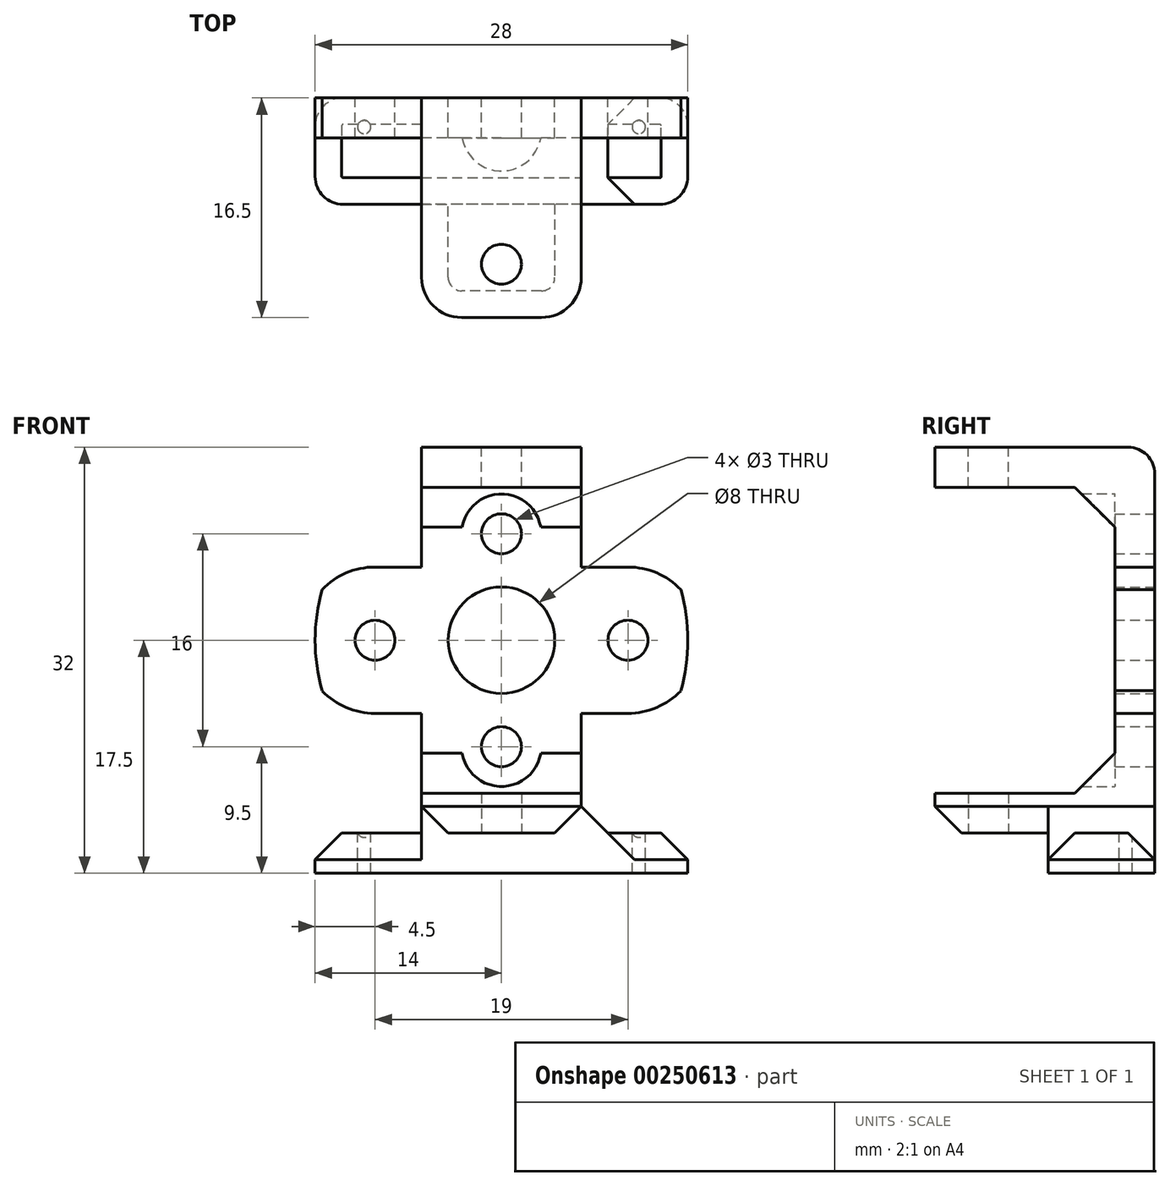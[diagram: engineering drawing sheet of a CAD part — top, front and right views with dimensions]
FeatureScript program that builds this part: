
annotation { "Feature Type Name" : "Feature", "Feature Type Description" : "" }
export const myFeature = defineFeature(function(context is Context, id is Id, definition is map)
    precondition{}
    {
        {
            var Q0;
            Q0=qCreatedBy(makeId("Front.planeOp"),FACE);
            var sketch = newSketch(context, id + "F0", { "sketchPlane" : qUnion([Q0])});
            skCircle(sketch, "E0", {"center": v(0, 0) * mm, "radius": 4.5 * mm});
            skCircle(sketch, "E1", {"center": v(9.5, 0) * mm, "radius": 1.5 * mm});
            skCircle(sketch, "E2.MirrorC", {"center": v(-9.5, 0) * mm, "radius": 1.5 * mm});
            skArc(sketch, "E3.0", {"start": v(9.5, -5.5) * mm, "mid": v(11.66, -5.06) * mm, "end": v(13.47, -3.8) * mm});
            skLineSegment(sketch, "E4", {"start": v(9.5, 7.45) * mm, "end": v(9.5, -7.59) * mm, "construction": true});
            skLineSegment(sketch, "E5", {"start": v(9.5, -5.5) * mm, "end": v(0, -5.5) * mm});
            skLineSegment(sketch, "E6.MirrorCS", {"start": v(9.5, 5.5) * mm, "end": v(0, 5.5) * mm});
            skArc(sketch, "E7.MirrorCS", {"start": v(-9.5, -5.5) * mm, "mid": v(-11.66, -5.06) * mm, "end": v(-13.47, -3.8) * mm});
            skLineSegment(sketch, "E8.MirrorCS", {"start": v(-9.5, 5.5) * mm, "end": v(0, 5.5) * mm});
            skLineSegment(sketch, "E9.MirrorCS", {"start": v(-9.5, -5.5) * mm, "end": v(0, -5.5) * mm});
            skArc(sketch, "E10", {"start": v(-13.47, 3.8) * mm, "mid": v(-14, 0) * mm, "end": v(-13.47, -3.8) * mm});
            skArc(sketch, "E11.trimOffspring", {"start": v(13.47, -3.8) * mm, "mid": v(14, 0) * mm, "end": v(13.47, 3.8) * mm});
            skArc(sketch, "E12.trimOffspring", {"start": v(-13.47, 3.8) * mm, "mid": v(-11.66, 5.06) * mm, "end": v(-9.5, 5.5) * mm});
            skArc(sketch, "E13.trimOffspring", {"start": v(13.47, 3.8) * mm, "mid": v(11.66, 5.06) * mm, "end": v(9.5, 5.5) * mm});
            skSolve(sketch);
        }
        {
            var Q0;
            Q0=qSketchRegion(id+"F0",true);
            extrude(context, id + "F1", {"entities" : qUnion([Q0]), "depth" : 3 * mm});
        }
        {
            var Q0;
            Q0=makeQuery(id+"F1.opExtrude","CAP_FACE",FACE,{"disambiguationData":[OSD([sQuery(id+"F0.wireOp",EDGE,"E0"),sQuery(id+"F0.wireOp",EDGE,"E1"),sQuery(id+"F0.wireOp",EDGE,"E2.MirrorC"),sQuery(id+"F0.wireOp",EDGE,"E3.0"),sQuery(id+"F0.wireOp",EDGE,"E5"),sQuery(id+"F0.wireOp",EDGE,"E6.MirrorCS"),sQuery(id+"F0.wireOp",EDGE,"E7.MirrorCS"),sQuery(id+"F0.wireOp",EDGE,"E8.MirrorCS"),sQuery(id+"F0.wireOp",EDGE,"E9.MirrorCS")])],"isStart":false});
            var sketch = newSketch(context, id + "F2", { "sketchPlane" : qUnion([Q0])});
            skLineSegment(sketch, "E14.rect.bottom", {"start": v(6, -14.5) * mm, "end": v(-6, -14.5) * mm});
            skLineSegment(sketch, "E14.rect.top", {"start": v(6, 14.5) * mm, "end": v(-6, 14.5) * mm});
            skLineSegment(sketch, "E14.rect.left", {"start": v(6, -14.5) * mm, "end": v(6, 14.5) * mm});
            skLineSegment(sketch, "E14.rect.right", {"start": v(-6, -14.5) * mm, "end": v(-6, 14.5) * mm});
            skPoint(sketch, "E14.rect.middle", {"position": v(0, 0) * mm});
            skSolve(sketch);
        }
        {
            var Q0;
            Q0=qSketchRegion(id+"F2",true);
            extrude(context, id + "F3", {"entities" : qUnion([Q0]), "operationType" : NewBodyOperationType.ADD, "oppositeDirection" : true, "depth" : 3 * mm});
        }
        {
            var Q0;
            Q0=makeQuery(id+"F3.opExtrude","SWEPT_FACE",FACE,{"disambiguationData":[OSD([sQuery(id+"F2.wireOp",EDGE,"E14.rect.bottom")])]});
            var sketch = newSketch(context, id + "F4", { "sketchPlane" : qUnion([Q0])});
            skLineSegment(sketch, "E15.bottom", {"start": v(-6, 0) * mm, "end": v(6, 0) * mm, "construction": true});
            skCircle(sketch, "E16", {"center": v(0, 12.5) * mm, "radius": 1.5 * mm});
            skLineSegment(sketch, "E17.bottom", {"start": v(-6, 0) * mm, "end": v(6, 0) * mm});
            skLineSegment(sketch, "E17.top", {"start": v(-3, 16.5) * mm, "end": v(3, 16.5) * mm});
            skLineSegment(sketch, "E17.left", {"start": v(-6, 0) * mm, "end": v(-6, 13.5) * mm});
            skLineSegment(sketch, "E17.right", {"start": v(6, 0) * mm, "end": v(6, 13.5) * mm});
            skPoint(sketch, "E18.visualSharp", {"position": v(-6, 16.5) * mm});
            skArc(sketch, "E18.filletArc", {"start": v(-3, 16.5) * mm, "mid": v(-5.12, 15.62) * mm, "end": v(-6, 13.5) * mm});
            skPoint(sketch, "E19.visualSharp", {"position": v(6, 16.5) * mm});
            skArc(sketch, "E19.filletArc", {"start": v(6, 13.5) * mm, "mid": v(5.12, 15.62) * mm, "end": v(3, 16.5) * mm});
            skSolve(sketch);
        }
        {
            var Q0;
            Q0=qSketchRegion(id+"F4",true);
            extrude(context, id + "F5", {"entities" : qUnion([Q0]), "oppositeDirection" : true, "depth" : 3 * mm});
        }
        {
            var Q0;
            Q0=makeQuery(id+"F3.boolean.opBoolean","MERGE",FACE,{"derivedFrom":[makeQuery(id+"F1.opExtrude","CAP_FACE",FACE,{"disambiguationData":[OSD([sQuery(id+"F0.wireOp",EDGE,"E0"),sQuery(id+"F0.wireOp",EDGE,"E1"),sQuery(id+"F0.wireOp",EDGE,"E2.MirrorC"),sQuery(id+"F0.wireOp",EDGE,"E3.0"),sQuery(id+"F0.wireOp",EDGE,"E5"),sQuery(id+"F0.wireOp",EDGE,"E6.MirrorCS"),sQuery(id+"F0.wireOp",EDGE,"E7.MirrorCS"),sQuery(id+"F0.wireOp",EDGE,"E8.MirrorCS"),sQuery(id+"F0.wireOp",EDGE,"E9.MirrorCS")])],"isStart":true}),makeQuery(id+"F3.opExtrude","CAP_FACE",FACE,{"disambiguationData":[OSD([sQuery(id+"F2.wireOp",EDGE,"E14.rect.bottom"),sQuery(id+"F2.wireOp",EDGE,"E14.rect.top"),sQuery(id+"F2.wireOp",EDGE,"E14.rect.left"),sQuery(id+"F2.wireOp",EDGE,"E14.rect.right")])],"isStart":false})]});
            var sketch = newSketch(context, id + "F6", { "sketchPlane" : qUnion([Q0])});
            skCircle(sketch, "E20", {"center": v(0, 0) * mm, "radius": 4 * mm});
            skCircle(sketch, "E21", {"center": v(0, 8) * mm, "radius": 1.5 * mm});
            skCircle(sketch, "E22.MirrorC", {"center": v(0, -8) * mm, "radius": 1.5 * mm});
            skSolve(sketch);
        }
        {
            var Q0;
            Q0=qSketchRegion(id+"F6",true);
            extrude(context, id + "F7", {"entities" : qUnion([Q0]), "operationType" : NewBodyOperationType.REMOVE, "endBound" : BoundingType.UP_TO_NEXT, "oppositeDirection" : true, "depth" : 25 * mm});
        }
        {
            var Q0;
            Q0=makeQuery(id+"F5.opExtrude","SWEPT_BODY",BODY,{"disambiguationData":[OSD([sQuery(id+"F4.wireOp",EDGE,"E16"),sQuery(id+"F4.wireOp",EDGE,"E17.bottom"),sQuery(id+"F4.wireOp",EDGE,"E17.top"),sQuery(id+"F4.wireOp",EDGE,"E17.left"),sQuery(id+"F4.wireOp",EDGE,"E17.right"),sQuery(id+"F4.wireOp",EDGE,"E18.filletArc"),sQuery(id+"F4.wireOp",EDGE,"E19.filletArc")])]});
            var Q1;
            Q1=qCreatedBy(makeId("Top.planeOp"),FACE);
            mirror(context, id + "F8", {"operationType" : NewBodyOperationType.ADD, "entities" : qUnion([Q0]), "mirrorPlane" : qUnion([Q1])});
        }
        {
            var Q0;
            Q0=makeQuery(id+"F3.opExtrude","CAP_EDGE",EDGE,{"disambiguationData":[OSD([sQuery(id+"F2.wireOp",EDGE,"E14.rect.top")])],"isStart":false});
            fillet(context, id + "F9", {"entities" : qUnion([Q0]), "radius" : 2 * mm, "tangentPropagation" : true, "allowEdgeOverflow" : false});
        }
        {
            var Q0;
            Q0=makeQuery(id+"F8.boolean.opBoolean","INTERSECT",EDGE,{"derivedFrom":[makeQuery(id+"F3.boolean.opBoolean","MERGE",FACE,{"derivedFrom":[makeQuery(id+"F1.opExtrude","CAP_FACE",FACE,{"disambiguationData":[OSD([sQuery(id+"F0.wireOp",EDGE,"E0"),sQuery(id+"F0.wireOp",EDGE,"E1"),sQuery(id+"F0.wireOp",EDGE,"E2.MirrorC"),sQuery(id+"F0.wireOp",EDGE,"E3.0"),sQuery(id+"F0.wireOp",EDGE,"E5"),sQuery(id+"F0.wireOp",EDGE,"E6.MirrorCS"),sQuery(id+"F0.wireOp",EDGE,"E7.MirrorCS"),sQuery(id+"F0.wireOp",EDGE,"E8.MirrorCS"),sQuery(id+"F0.wireOp",EDGE,"E9.MirrorCS"),sQuery(id+"F0.wireOp",EDGE,"E10"),sQuery(id+"F0.wireOp",EDGE,"E11.trimOffspring"),sQuery(id+"F0.wireOp",EDGE,"E12.trimOffspring"),sQuery(id+"F0.wireOp",EDGE,"E13.trimOffspring")])],"isStart":false}),makeQuery(id+"F3.opExtrude","CAP_FACE",FACE,{"disambiguationData":[OSD([sQuery(id+"F2.wireOp",EDGE,"E14.rect.bottom"),sQuery(id+"F2.wireOp",EDGE,"E14.rect.top"),sQuery(id+"F2.wireOp",EDGE,"E14.rect.left"),sQuery(id+"F2.wireOp",EDGE,"E14.rect.right")])],"isStart":true})]}),makeQuery(id+"F8.opPattern","COPY",FACE,{"derivedFrom":makeQuery(id+"F5.opExtrude","CAP_FACE",FACE,{"disambiguationData":[OSD([sQuery(id+"F4.wireOp",EDGE,"E16"),sQuery(id+"F4.wireOp",EDGE,"E17.bottom"),sQuery(id+"F4.wireOp",EDGE,"E17.top"),sQuery(id+"F4.wireOp",EDGE,"E17.left"),sQuery(id+"F4.wireOp",EDGE,"E17.right"),sQuery(id+"F4.wireOp",EDGE,"E18.filletArc"),sQuery(id+"F4.wireOp",EDGE,"E19.filletArc")])],"isStart":false}),"instanceName":"1"})]});
            var Q1;
            Q1=makeQuery(id+"F8.boolean.opBoolean","INTERSECT",EDGE,{"derivedFrom":[makeQuery(id+"F5.opExtrude","CAP_FACE",FACE,{"disambiguationData":[OSD([sQuery(id+"F4.wireOp",EDGE,"E16"),sQuery(id+"F4.wireOp",EDGE,"E17.bottom"),sQuery(id+"F4.wireOp",EDGE,"E17.top"),sQuery(id+"F4.wireOp",EDGE,"E17.left"),sQuery(id+"F4.wireOp",EDGE,"E17.right"),sQuery(id+"F4.wireOp",EDGE,"E18.filletArc"),sQuery(id+"F4.wireOp",EDGE,"E19.filletArc")])],"isStart":false}),makeQuery(id+"F3.boolean.opBoolean","MERGE",FACE,{"derivedFrom":[makeQuery(id+"F1.opExtrude","CAP_FACE",FACE,{"disambiguationData":[OSD([sQuery(id+"F0.wireOp",EDGE,"E0"),sQuery(id+"F0.wireOp",EDGE,"E1"),sQuery(id+"F0.wireOp",EDGE,"E2.MirrorC"),sQuery(id+"F0.wireOp",EDGE,"E3.0"),sQuery(id+"F0.wireOp",EDGE,"E5"),sQuery(id+"F0.wireOp",EDGE,"E6.MirrorCS"),sQuery(id+"F0.wireOp",EDGE,"E7.MirrorCS"),sQuery(id+"F0.wireOp",EDGE,"E8.MirrorCS"),sQuery(id+"F0.wireOp",EDGE,"E9.MirrorCS"),sQuery(id+"F0.wireOp",EDGE,"E10"),sQuery(id+"F0.wireOp",EDGE,"E11.trimOffspring"),sQuery(id+"F0.wireOp",EDGE,"E12.trimOffspring"),sQuery(id+"F0.wireOp",EDGE,"E13.trimOffspring")])],"isStart":false}),makeQuery(id+"F3.opExtrude","CAP_FACE",FACE,{"disambiguationData":[OSD([sQuery(id+"F2.wireOp",EDGE,"E14.rect.bottom"),sQuery(id+"F2.wireOp",EDGE,"E14.rect.top"),sQuery(id+"F2.wireOp",EDGE,"E14.rect.left"),sQuery(id+"F2.wireOp",EDGE,"E14.rect.right")])],"isStart":true})]})]});
            chamfer(context, id + "F10", {"entities" : qUnion([Q0, Q1]), "width" : 3 * mm, "tangentPropagation" : true});
        }
        {
            var Q0;
            Q0=makeQuery(id+"F3.boolean.opBoolean","MERGE",FACE,{"derivedFrom":[makeQuery(id+"F1.opExtrude","CAP_FACE",FACE,{"disambiguationData":[OSD([sQuery(id+"F0.wireOp",EDGE,"E0"),sQuery(id+"F0.wireOp",EDGE,"E1"),sQuery(id+"F0.wireOp",EDGE,"E2.MirrorC"),sQuery(id+"F0.wireOp",EDGE,"E3.0"),sQuery(id+"F0.wireOp",EDGE,"E5"),sQuery(id+"F0.wireOp",EDGE,"E6.MirrorCS"),sQuery(id+"F0.wireOp",EDGE,"E7.MirrorCS"),sQuery(id+"F0.wireOp",EDGE,"E8.MirrorCS"),sQuery(id+"F0.wireOp",EDGE,"E9.MirrorCS"),sQuery(id+"F0.wireOp",EDGE,"E10"),sQuery(id+"F0.wireOp",EDGE,"E11.trimOffspring"),sQuery(id+"F0.wireOp",EDGE,"E12.trimOffspring"),sQuery(id+"F0.wireOp",EDGE,"E13.trimOffspring")])],"isStart":false}),makeQuery(id+"F3.opExtrude","CAP_FACE",FACE,{"disambiguationData":[OSD([sQuery(id+"F2.wireOp",EDGE,"E14.rect.bottom"),sQuery(id+"F2.wireOp",EDGE,"E14.rect.top"),sQuery(id+"F2.wireOp",EDGE,"E14.rect.left"),sQuery(id+"F2.wireOp",EDGE,"E14.rect.right")])],"isStart":true})]});
            var sketch = newSketch(context, id + "F11", { "sketchPlane" : qUnion([Q0])});
            skCircle(sketch, "E23", {"center": v(0, 8) * mm, "radius": 3 * mm});
            skCircle(sketch, "E24.MirrorC", {"center": v(0, -8) * mm, "radius": 3 * mm});
            skSolve(sketch);
        }
        {
            var Q0;
            Q0=qSketchRegion(id+"F11",true);
            var Q1;
            {var subQ0=sQuery(id+"F2.wireOp",EDGE,"E14.rect.right");var subQ1=sQuery(id+"F2.wireOp",EDGE,"E14.rect.left");var subQ2=sQuery(id+"F2.wireOp",EDGE,"E14.rect.top");var subQ3=sQuery(id+"F2.wireOp",EDGE,"E14.rect.bottom");var subQ4=sQuery(id+"F0.wireOp",EDGE,"E13.trimOffspring");var subQ5=sQuery(id+"F0.wireOp",EDGE,"E12.trimOffspring");var subQ6=sQuery(id+"F0.wireOp",EDGE,"E11.trimOffspring");var subQ7=sQuery(id+"F0.wireOp",EDGE,"E10");var subQ8=sQuery(id+"F0.wireOp",EDGE,"E9.MirrorCS");var subQ9=sQuery(id+"F0.wireOp",EDGE,"E8.MirrorCS");var subQ10=sQuery(id+"F0.wireOp",EDGE,"E7.MirrorCS");var subQ11=sQuery(id+"F0.wireOp",EDGE,"E6.MirrorCS");var subQ12=sQuery(id+"F0.wireOp",EDGE,"E5");var subQ13=sQuery(id+"F0.wireOp",EDGE,"E3.0");var subQ14=sQuery(id+"F0.wireOp",EDGE,"E2.MirrorC");var subQ15=sQuery(id+"F0.wireOp",EDGE,"E1");var subQ16=sQuery(id+"F0.wireOp",EDGE,"E0");var subQ17=sQuery(id+"F4.wireOp",EDGE,"E19.filletArc");var subQ18=sQuery(id+"F4.wireOp",EDGE,"E18.filletArc");var subQ19=sQuery(id+"F4.wireOp",EDGE,"E17.right");var subQ20=sQuery(id+"F4.wireOp",EDGE,"E17.left");var subQ21=sQuery(id+"F4.wireOp",EDGE,"E17.top");var subQ22=sQuery(id+"F4.wireOp",EDGE,"E17.bottom");var subQ23=sQuery(id+"F4.wireOp",EDGE,"E16");Q1=makeQuery(id+"F10.opChamfer","BLEND_FACE",FACE,{"disambiguationData":[OSD([subQ16,subQ15,subQ14,subQ13,subQ12,subQ11,subQ10,subQ9,subQ8,subQ7,subQ6,subQ5,subQ4,subQ3,subQ2,subQ1,subQ0,subQ23,subQ22,subQ21,subQ20,subQ19,subQ18,subQ17]),TDD([makeQuery(id+"F8.boolean.opBoolean","INTERSECT",EDGE,{"derivedFrom":[makeQuery(id+"F5.opExtrude","CAP_FACE",FACE,{"disambiguationData":[OSD([subQ23,subQ22,subQ21,subQ20,subQ19,subQ18,subQ17])],"isStart":false}),makeQuery(id+"F3.boolean.opBoolean","MERGE",FACE,{"derivedFrom":[makeQuery(id+"F1.opExtrude","CAP_FACE",FACE,{"disambiguationData":[OSD([subQ16,subQ15,subQ14,subQ13,subQ12,subQ11,subQ10,subQ9,subQ8,subQ7,subQ6,subQ5,subQ4])],"isStart":false}),makeQuery(id+"F3.opExtrude","CAP_FACE",FACE,{"disambiguationData":[OSD([subQ3,subQ2,subQ1,subQ0])],"isStart":true})]})]})])]});}
            extrude(context, id + "F12", {"entities" : qUnion([Q0]), "operationType" : NewBodyOperationType.REMOVE, "endBoundEntityFace" : qUnion([Q1]), "depth" : 4 * mm});
        }
        {
            var Q0;
            Q0=makeQuery(id+"F8.boolean.opBoolean","MERGE",FACE,{"derivedFrom":[makeQuery(id+"F3.opExtrude","SWEPT_FACE",FACE,{"disambiguationData":[OSD([sQuery(id+"F2.wireOp",EDGE,"E14.rect.bottom")])]}),makeQuery(id+"F5.opExtrude","CAP_FACE",FACE,{"disambiguationData":[OSD([sQuery(id+"F4.wireOp",EDGE,"E16"),sQuery(id+"F4.wireOp",EDGE,"E17.bottom"),sQuery(id+"F4.wireOp",EDGE,"E17.top"),sQuery(id+"F4.wireOp",EDGE,"E17.left"),sQuery(id+"F4.wireOp",EDGE,"E17.right"),sQuery(id+"F4.wireOp",EDGE,"E18.filletArc"),sQuery(id+"F4.wireOp",EDGE,"E19.filletArc")])],"isStart":true})]});
            var sketch = newSketch(context, id + "F13", { "sketchPlane" : qUnion([Q0])});
            skLineSegment(sketch, "E25.bottom", {"start": v(6, 0) * mm, "end": v(-11.9, 0) * mm});
            skLineSegment(sketch, "E25.top", {"start": v(6, 8) * mm, "end": v(-11.9, 8) * mm});
            skLineSegment(sketch, "E25.left", {"start": v(6, 0) * mm, "end": v(6, 8) * mm});
            skLineSegment(sketch, "E25.right", {"start": v(-14, 2.1) * mm, "end": v(-14, 5.9) * mm});
            skLineSegment(sketch, "E26", {"start": v(0, 12.5) * mm, "end": v(-18.5, -6) * mm, "construction": true});
            skCircle(sketch, "E27", {"center": v(-10.32, 2.18) * mm, "radius": 0.5 * mm});
            skPoint(sketch, "E28.visualSharp", {"position": v(-14, 8) * mm});
            skArc(sketch, "E28.filletArc", {"start": v(-11.9, 8) * mm, "mid": v(-13.38, 7.38) * mm, "end": v(-14, 5.9) * mm});
            skPoint(sketch, "E29.visualSharp", {"position": v(-14, 0) * mm});
            skArc(sketch, "E29.filletArc", {"start": v(-14, 2.1) * mm, "mid": v(-13.38, 0.62) * mm, "end": v(-11.9, 0) * mm});
            skArc(sketch, "E30.MirrorCS", {"start": v(14, 2.1) * mm, "mid": v(13.38, 0.62) * mm, "end": v(11.9, 0) * mm});
            skLineSegment(sketch, "E31.MirrorCS", {"start": v(14, 2.1) * mm, "end": v(14, 5.9) * mm});
            skArc(sketch, "E32.MirrorCS", {"start": v(11.9, 8) * mm, "mid": v(13.38, 7.38) * mm, "end": v(14, 5.9) * mm});
            skLineSegment(sketch, "E33", {"start": v(11.9, 0) * mm, "end": v(6, 0) * mm});
            skLineSegment(sketch, "E34", {"start": v(11.9, 8) * mm, "end": v(6, 8) * mm});
            skCircle(sketch, "E35.MirrorC", {"center": v(10.32, 2.18) * mm, "radius": 0.5 * mm});
            skSolve(sketch);
        }
        {
            var Q0;
            Q0=qSketchRegion(id+"F13",true);
            extrude(context, id + "F14", {"entities" : qUnion([Q0]), "operationType" : NewBodyOperationType.ADD, "depth" : 3 * mm});
        }
        {
            var Q0;
            {var subQ0=sQuery(id+"F2.wireOp",EDGE,"E14.rect.right");var subQ1=sQuery(id+"F2.wireOp",EDGE,"E14.rect.bottom");var subQ3=sQuery(id+"F13.wireOp",EDGE,"E25.bottom");var subQ4=sQuery(id+"F4.wireOp",EDGE,"E17.left");Q0=makeQuery(id+"F14.boolean.opBoolean","SPLIT",EDGE,{"disambiguationData":[TD([makeQuery(id+"F14.opExtrude","SWEPT_FACE",FACE,{"disambiguationData":[OSD([subQ3])]})])],"derivedFrom":makeQuery(id+"F8.boolean.opBoolean","MERGE",EDGE,{"derivedFrom":[makeQuery(id+"F3.opExtrude","SWEPT_EDGE",EDGE,{"disambiguationData":[OSD([subQ1,subQ0])]}),makeQuery(id+"F5.opExtrude","CAP_EDGE",EDGE,{"disambiguationData":[OSD([subQ4])],"isStart":true})]})});}
            chamfer(context, id + "F15", {"entities" : qUnion([Q0]), "width" : 2 * mm, "tangentPropagation" : true});
        }
        {
            var Q0;
            {var subQ0=sQuery(id+"F2.wireOp",EDGE,"E14.rect.left");var subQ1=sQuery(id+"F4.wireOp",EDGE,"E17.right");var subQ2=sQuery(id+"F2.wireOp",EDGE,"E14.rect.bottom");var subQ3=sQuery(id+"F13.wireOp",EDGE,"E33");var subQ4=sQuery(id+"F13.wireOp",EDGE,"E25.bottom");Q0=makeQuery(id+"F14.boolean.opBoolean","SPLIT",EDGE,{"disambiguationData":[TD([makeQuery(id+"F14.opExtrude","SWEPT_FACE",FACE,{"disambiguationData":[OSD([subQ4,subQ3])]})])],"derivedFrom":makeQuery(id+"F8.boolean.opBoolean","MERGE",EDGE,{"derivedFrom":[makeQuery(id+"F3.opExtrude","SWEPT_EDGE",EDGE,{"disambiguationData":[OSD([subQ2,subQ0])]}),makeQuery(id+"F5.opExtrude","CAP_EDGE",EDGE,{"disambiguationData":[OSD([subQ1])],"isStart":true})]})});}
            chamfer(context, id + "F16", {"entities" : qUnion([Q0]), "width" : 2 * mm, "tangentPropagation" : true});
        }
        {
            var Q0;
            {var subQ0=sQuery(id+"F4.wireOp",EDGE,"E17.right");var subQ1=sQuery(id+"F4.wireOp",EDGE,"E17.left");var subQ2=sQuery(id+"F13.wireOp",EDGE,"E34");var subQ3=sQuery(id+"F13.wireOp",EDGE,"E25.top");Q0=makeQuery(id+"F14.boolean.opBoolean","SPLIT",EDGE,{"disambiguationData":[TD([makeQuery(id+"F3.opExtrude","SWEPT_FACE",FACE,{"disambiguationData":[OSD([sQuery(id+"F2.wireOp",EDGE,"E14.rect.bottom")])]}),makeQuery(id+"F3.opExtrude","SWEPT_FACE",FACE,{"disambiguationData":[OSD([sQuery(id+"F2.wireOp",EDGE,"E14.rect.left")])]}),makeQuery(id+"F3.opExtrude","SWEPT_FACE",FACE,{"disambiguationData":[OSD([sQuery(id+"F2.wireOp",EDGE,"E14.rect.right")])]}),makeQuery(id+"F5.opExtrude","CAP_FACE",FACE,{"disambiguationData":[OSD([sQuery(id+"F4.wireOp",EDGE,"E16"),sQuery(id+"F4.wireOp",EDGE,"E17.bottom"),sQuery(id+"F4.wireOp",EDGE,"E17.top"),subQ1,subQ0,sQuery(id+"F4.wireOp",EDGE,"E18.filletArc"),sQuery(id+"F4.wireOp",EDGE,"E19.filletArc")])],"isStart":true}),makeQuery(id+"F5.opExtrude","SWEPT_FACE",FACE,{"disambiguationData":[OSD([subQ1])]}),makeQuery(id+"F5.opExtrude","SWEPT_FACE",FACE,{"disambiguationData":[OSD([subQ0])]}),makeQuery(id+"F14.opExtrude","CAP_FACE",FACE,{"disambiguationData":[OSD([sQuery(id+"F13.wireOp",EDGE,"E25.bottom"),subQ3,sQuery(id+"F13.wireOp",EDGE,"E25.right"),sQuery(id+"F13.wireOp",EDGE,"E27"),sQuery(id+"F13.wireOp",EDGE,"E28.filletArc"),sQuery(id+"F13.wireOp",EDGE,"E29.filletArc"),sQuery(id+"F13.wireOp",EDGE,"E30.MirrorCS"),sQuery(id+"F13.wireOp",EDGE,"E31.MirrorCS"),sQuery(id+"F13.wireOp",EDGE,"E32.MirrorCS"),sQuery(id+"F13.wireOp",EDGE,"E33"),subQ2])],"isStart":true}),makeQuery(id+"F14.opExtrude","SWEPT_FACE",FACE,{"disambiguationData":[OSD([subQ3,subQ2])]})])],"derivedFrom":makeQuery(id+"F14.opExtrude","CAP_EDGE",EDGE,{"disambiguationData":[OSD([subQ3,subQ2])],"isStart":true})});}
            chamfer(context, id + "F17", {"entities" : qUnion([Q0]), "width" : 2 * mm, "tangentPropagation" : true});
        }
    });
